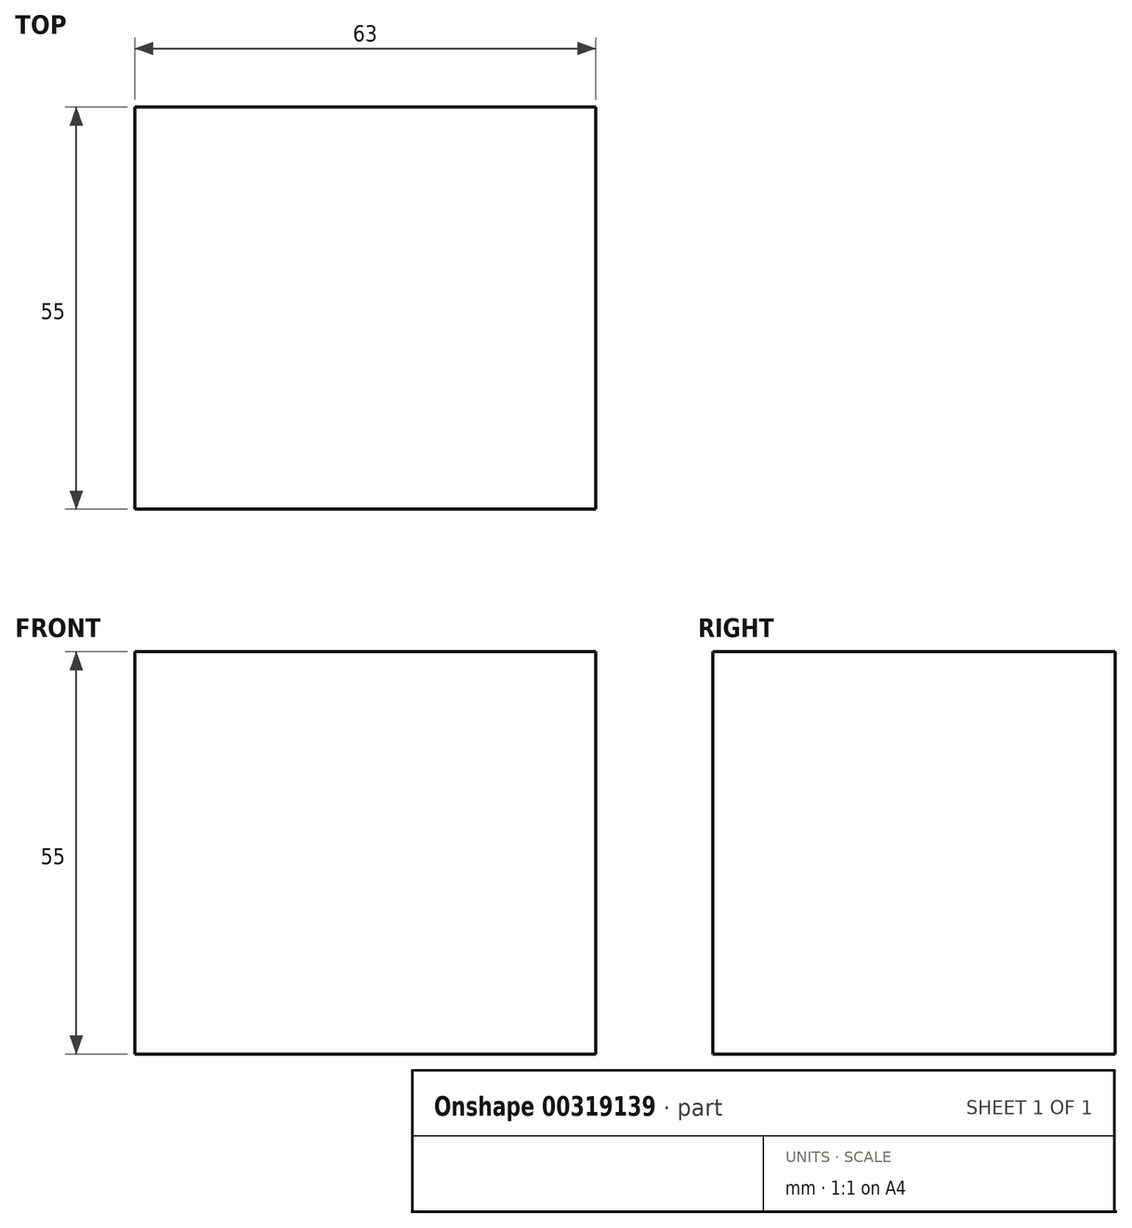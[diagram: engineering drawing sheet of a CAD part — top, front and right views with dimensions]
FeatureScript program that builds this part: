
annotation { "Feature Type Name" : "Feature", "Feature Type Description" : "" }
export const myFeature = defineFeature(function(context is Context, id is Id, definition is map)
    precondition{}
    {
        {
            var Q0;
            Q0=qCreatedBy(makeId("Right.planeOp"),FACE);
            var sketch = newSketch(context, id + "F0", { "sketchPlane" : qUnion([Q0])});
            skLineSegment(sketch, "E0.bottom", {"start": v(71.02, 69.2) * mm, "end": v(126.02, 69.2) * mm});
            skLineSegment(sketch, "E0.top", {"start": v(71.02, 14.2) * mm, "end": v(126.02, 14.2) * mm});
            skLineSegment(sketch, "E0.left", {"start": v(71.02, 69.2) * mm, "end": v(71.02, 14.2) * mm});
            skLineSegment(sketch, "E0.right", {"start": v(126.02, 69.2) * mm, "end": v(126.02, 14.2) * mm});
            skSolve(sketch);
        }
        {
            var Q0;
            Q0=makeQuery(id+"F0.imprint","IMPRINT",FACE,{"disambiguationData":[TD([[makeQuery(id+"F0.imprint","IMPRINT",EDGE,{"derivedFrom":sQuery(id+"F0.wireOp",EDGE,"4e0974c8-6d19-4d54-91bd-13c7d9c95e3d.bottom")}),-1.0]])]});
            var Q1;
            Q1=makeQuery(id+"F0.imprint","IMPRINT",FACE,{"disambiguationData":[TD([[makeQuery(id+"F0.imprint","IMPRINT",EDGE,{"derivedFrom":sQuery(id+"F0.wireOp",EDGE,"E0.bottom")}),-1.0]])]});
            extrude(context, id + "F1", {"entities" : qUnion([Q0, Q1]), "depth" : 63 * mm});
        }
    });
